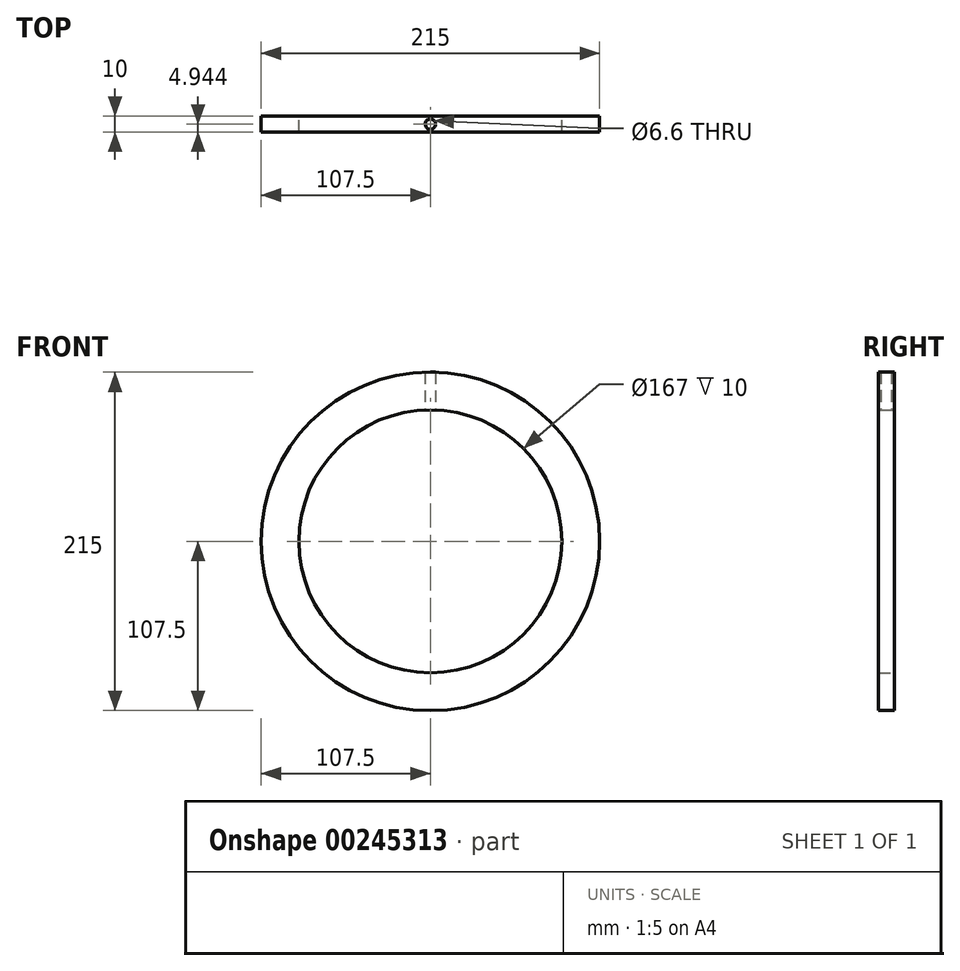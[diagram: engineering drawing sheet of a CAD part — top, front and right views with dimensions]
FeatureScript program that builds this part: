
annotation { "Feature Type Name" : "Feature", "Feature Type Description" : "" }
export const myFeature = defineFeature(function(context is Context, id is Id, definition is map)
    precondition{}
    {
        {
            var Q0;
            Q0=qCreatedBy(makeId("Front.planeOp"),FACE);
            var sketch = newSketch(context, id + "F0", { "sketchPlane" : qUnion([Q0])});
            skCircle(sketch, "E0", {"center": v(0, 0) * mm, "radius": 83.5 * mm});
            skCircle(sketch, "E1", {"center": v(0, 0) * mm, "radius": 107.5 * mm});
            skSolve(sketch);
        }
        {
            var Q0;
            Q0=makeQuery(id+"F0.imprint","IMPRINT",FACE,{"disambiguationData":[TD([[makeQuery(id+"F0.imprint","IMPRINT",EDGE,{"derivedFrom":sQuery(id+"F0.wireOp",EDGE,"E0")}),-1.0]])]});
            extrude(context, id + "F1", {"entities" : qUnion([Q0]), "depth" : 10 * mm, "offsetDistance" : 25 * mm});
        }
        {
            var Q0;
            Q0=qCreatedBy(makeId("Top.planeOp"),FACE);
            var sketch = newSketch(context, id + "F2", { "sketchPlane" : qUnion([Q0])});
            skPoint(sketch, "E2", {"position": v(0, -5.06) * mm});
            skSolve(sketch);
        }
        {
            var Q0;
            Q0=sQuery(id+"F2.wireOp",VERTEX,"E2");
            var Q1;
            Q1=makeQuery(id+"F1.opExtrude","SWEPT_BODY",BODY,{"disambiguationData":[OSD([sQuery(id+"F0.wireOp",EDGE,"E0"),sQuery(id+"F0.wireOp",EDGE,"E1")])]});
            hole(context, id + "F3", {"style" : HoleStyle.C_BORE, "endStyle" : HoleEndStyle.THROUGH, "oppositeDirection" : true, "standardTappedOrClearance" : lookupTablePath({ "fit" : "Normal", "standard" : "ISO", "size" : "M6", "type" : "Clearance" }), "standardBlindInLast" : lookupTablePath({ "fit" : "Normal", "standard" : "ISO", "engagement" : "75%", "pitch" : "1 mm", "size" : "M6", "type" : "Clearance & tapped" }), "holeDiameter" : 6.6 * mm, "cBoreDiameter" : 11.25 * mm, "cBoreDepth" : 6 * mm, "majorDiameter" : 5 * mm, "isTappedThrough" : true, "tappedDepth" : 28 * mm, "tapClearance" : 3, "startFromSketch" : true, "locations" : qUnion([Q0]), "scope" : qUnion([Q1])});
        }
    });
